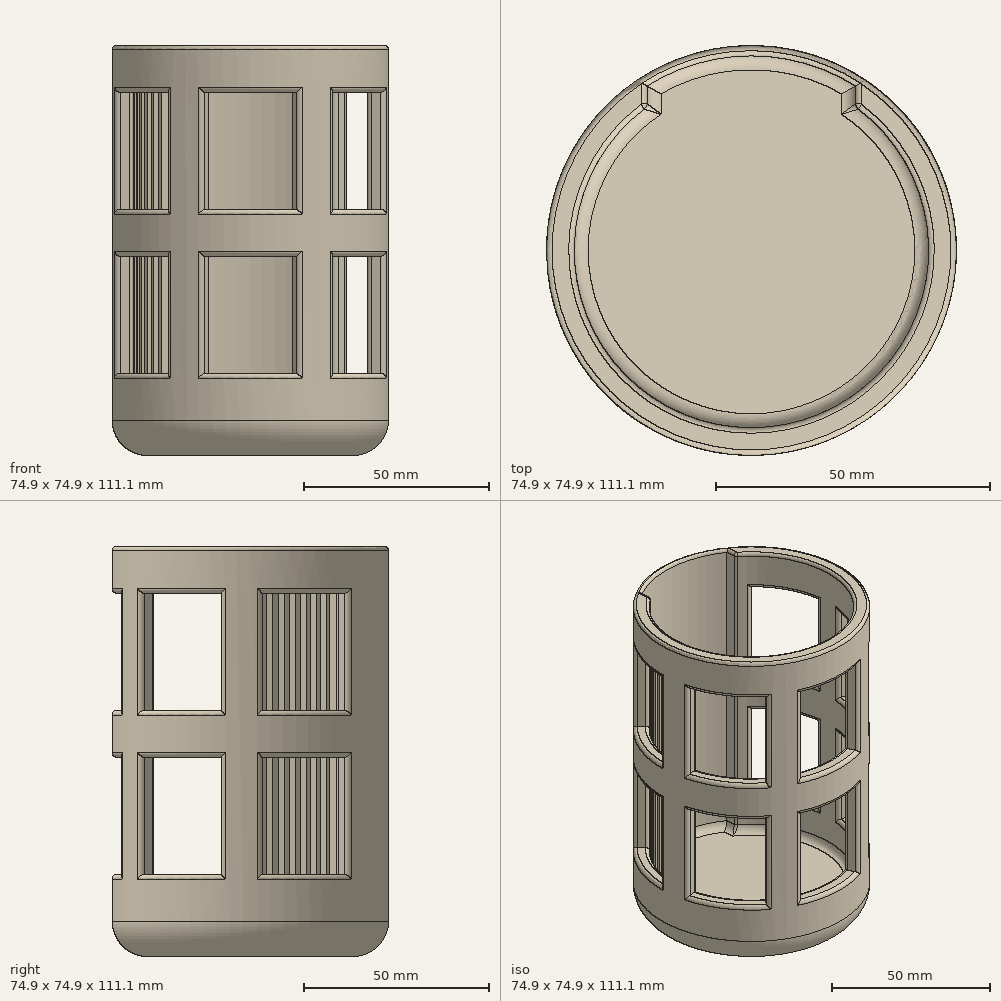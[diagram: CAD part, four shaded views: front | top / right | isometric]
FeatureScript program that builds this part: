
annotation { "Feature Type Name" : "Feature", "Feature Type Description" : "" }
export const myFeature = defineFeature(function(context is Context, id is Id, definition is map)
    precondition{}
    {
        {
            var Q0;
            Q0=qCreatedBy(makeId("Top.planeOp"),FACE);
            var sketch = newSketch(context, id + "F0", { "sketchPlane" : qUnion([Q0])});
            skCircle(sketch, "E0", {"center": v(0, 0) * mm, "radius": 37.47 * mm});
            skArc(sketch, "E1", {"start": v(-19.05, 26.19) * mm, "mid": v(0, -32.39) * mm, "end": v(19.05, 26.19) * mm});
            skArc(sketch, "E2", {"start": v(19.05, 30.03) * mm, "mid": v(0, 35.56) * mm, "end": v(-19.05, 30.03) * mm});
            skLineSegment(sketch, "E3", {"start": v(-19.05, 26.19) * mm, "end": v(-19.05, 30.03) * mm});
            skLineSegment(sketch, "E4", {"start": v(19.05, 26.19) * mm, "end": v(19.05, 30.03) * mm});
            skPoint(sketch, "E5.orphan", {"position": v(-19.05, 0) * mm});
            skPoint(sketch, "E6.orphan", {"position": v(19.05, 0) * mm});
            skSolve(sketch);
        }
        {
            var Q0;
            Q0 = qSketchRegion(id + "F0", true);
            extrude(context, id + "F1", {"entities" : qUnion([Q0]), "depth" : 101.6 * mm});
        }
        {
            var Q0;
            Q0=makeQuery(id+"F1.opExtrude","CAP_FACE",FACE,{"disambiguationData":[OSD([sQuery(id+"F0.wireOp",EDGE,"E0"),sQuery(id+"F0.wireOp",EDGE,"E1"),sQuery(id+"F0.wireOp",EDGE,"E2"),sQuery(id+"F0.wireOp",EDGE,"E3"),sQuery(id+"F0.wireOp",EDGE,"E4")])],"isStart":true});
            var sketch = newSketch(context, id + "F2", { "sketchPlane" : qUnion([Q0])});
            skCircle(sketch, "E7.0", {"center": v(0, 0) * mm, "radius": 37.47 * mm});
            skSolve(sketch);
        }
        {
            var Q0;
            Q0 = qSketchRegion(id + "F2", true);
            extrude(context, id + "F3", {"entities" : qUnion([Q0]), "operationType" : NewBodyOperationType.ADD, "depth" : 9.52 * mm});
        }
        {
            var Q0;
            Q0=makeQuery(id+"F3.opExtrude","CAP_EDGE",EDGE,{"disambiguationData":[OSD([sQuery(id+"F2.wireOp",EDGE,"E7.0")])],"isStart":false});
            fillet(context, id + "F4", {"entities" : qUnion([Q0]), "radius" : 9.52 * mm, "tangentPropagation" : true, "allowEdgeOverflow" : false});
        }
        {
            var Q0;
            Q0=makeQuery(id+"F1.opExtrude","CAP_FACE",FACE,{"disambiguationData":[OSD([sQuery(id+"F0.wireOp",EDGE,"E0"),sQuery(id+"F0.wireOp",EDGE,"E1"),sQuery(id+"F0.wireOp",EDGE,"E2"),sQuery(id+"F0.wireOp",EDGE,"E3"),sQuery(id+"F0.wireOp",EDGE,"E4")])],"isStart":false});
            fillet(context, id + "F5", {"entities" : qUnion([Q0]), "radius" : 1.02 * mm, "tangentPropagation" : true, "allowEdgeOverflow" : false});
        }
        {
            var Q0;
            Q0=makeQuery(id+"F3.opExtrude","CAP_FACE",FACE,{"disambiguationData":[OSD([sQuery(id+"F2.wireOp",EDGE,"E7.0")])],"isStart":true});
            fillet(context, id + "F6", {"entities" : qUnion([Q0]), "radius" : 2.54 * mm, "tangentPropagation" : true, "allowEdgeOverflow" : false});
        }
        {
            var Q0;
            Q0=qCreatedBy(makeId("Top.planeOp"),FACE);
            cPlane(context, id + "F7", {"entities" : qUnion([Q0]), "cplaneType" : CPlaneType.OFFSET, "offset" : 12.7 * mm, "width" : 152.4 * mm, "height" : 152.4 * mm});
        }
        {
            var Q0;
            Q0=qCreatedBy(id+"F7.planeOp",FACE);
            var sketch = newSketch(context, id + "F8", { "sketchPlane" : qUnion([Q0])});
            skLineSegment(sketch, "E8", {"start": v(0, 0) * mm, "end": v(-37.94, 37.94) * mm});
            skLineSegment(sketch, "E9", {"start": v(-37.94, 37.94) * mm, "end": v(-57.72, 5.05) * mm});
            skLineSegment(sketch, "E10", {"start": v(-57.72, 5.05) * mm, "end": v(0, 0) * mm});
            skLineSegment(sketch, "E11", {"start": v(0, 0) * mm, "end": v(-57.72, -12.8) * mm});
            skLineSegment(sketch, "E12", {"start": v(-57.72, -12.8) * mm, "end": v(-33.49, -43.64) * mm});
            skLineSegment(sketch, "E13", {"start": v(-33.49, -43.64) * mm, "end": v(0, 0) * mm});
            skLineSegment(sketch, "E14", {"start": v(0, 0) * mm, "end": v(-17.01, -46.74) * mm});
            skLineSegment(sketch, "E15", {"start": v(-17.01, -46.74) * mm, "end": v(17.03, -46.78) * mm});
            skLineSegment(sketch, "E16", {"start": v(17.03, -46.78) * mm, "end": v(0, 0) * mm});
            skLineSegment(sketch, "E17", {"start": v(0, 0) * mm, "end": v(29, -37.8) * mm});
            skLineSegment(sketch, "E18", {"start": v(29, -37.8) * mm, "end": v(48.74, -10.8) * mm});
            skLineSegment(sketch, "E19", {"start": v(48.74, -10.8) * mm, "end": v(0, 0) * mm});
            skLineSegment(sketch, "E20", {"start": v(0, 0) * mm, "end": v(33.33, 33.33) * mm});
            skLineSegment(sketch, "E21", {"start": v(33.33, 33.33) * mm, "end": v(45.53, 3.98) * mm});
            skLineSegment(sketch, "E22", {"start": v(45.53, 3.98) * mm, "end": v(0, 0) * mm});
            skSolve(sketch);
        }
        {
            var Q0;
            Q0 = qSketchRegion(id + "F8", true);
            extrude(context, id + "F9", {"entities" : qUnion([Q0]), "operationType" : NewBodyOperationType.REMOVE, "depth" : 76.2 * mm});
        }
        {
            var Q0;
            Q0=qCreatedBy(id+"F7.planeOp",FACE);
            cPlane(context, id + "F10", {"entities" : qUnion([Q0]), "cplaneType" : CPlaneType.OFFSET, "offset" : 31.75 * mm, "width" : 152.4 * mm, "height" : 152.4 * mm});
        }
        {
            var Q0;
            Q0=qCreatedBy(id+"F10.planeOp",FACE);
            var sketch = newSketch(context, id + "F11", { "sketchPlane" : qUnion([Q0])});
            skArc(sketch, "E23", {"start": v(-19.18, 32.18) * mm, "mid": v(0, -37.47) * mm, "end": v(19.18, 32.18) * mm});
            skArc(sketch, "E24", {"start": v(-19.18, 26.1) * mm, "mid": v(0, -32.39) * mm, "end": v(19.18, 26.1) * mm});
            skLineSegment(sketch, "E25", {"start": v(-19.18, 32.18) * mm, "end": v(-19.18, 26.1) * mm});
            skLineSegment(sketch, "E26", {"start": v(19.18, 32.18) * mm, "end": v(19.18, 26.1) * mm});
            skSolve(sketch);
        }
        {
            var Q0;
            Q0 = qSketchRegion(id + "F11", true);
            extrude(context, id + "F12", {"entities" : qUnion([Q0]), "operationType" : NewBodyOperationType.ADD, "depth" : 12.7 * mm});
        }
        {
            var Q0;
            Q0=makeQuery(id+"F3.boolean.opBoolean","MERGE",FACE,{"derivedFrom":[makeQuery(id+"F1.opExtrude","SWEPT_FACE",FACE,{"disambiguationData":[OSD([sQuery(id+"F0.wireOp",EDGE,"E0")])]}),makeQuery(id+"F3.opExtrude","SWEPT_FACE",FACE,{"disambiguationData":[OSD([sQuery(id+"F2.wireOp",EDGE,"E7.0")])]})]});
            var Q1;
            Q1=makeQuery(id+"F1.opExtrude","SWEPT_FACE",FACE,{"disambiguationData":[OSD([sQuery(id+"F0.wireOp",EDGE,"E1")])]});
            fillet(context, id + "F13", {"entities" : qUnion([Q0, Q1]), "radius" : 1.27 * mm, "tangentPropagation" : true, "allowEdgeOverflow" : false});
        }
    });
